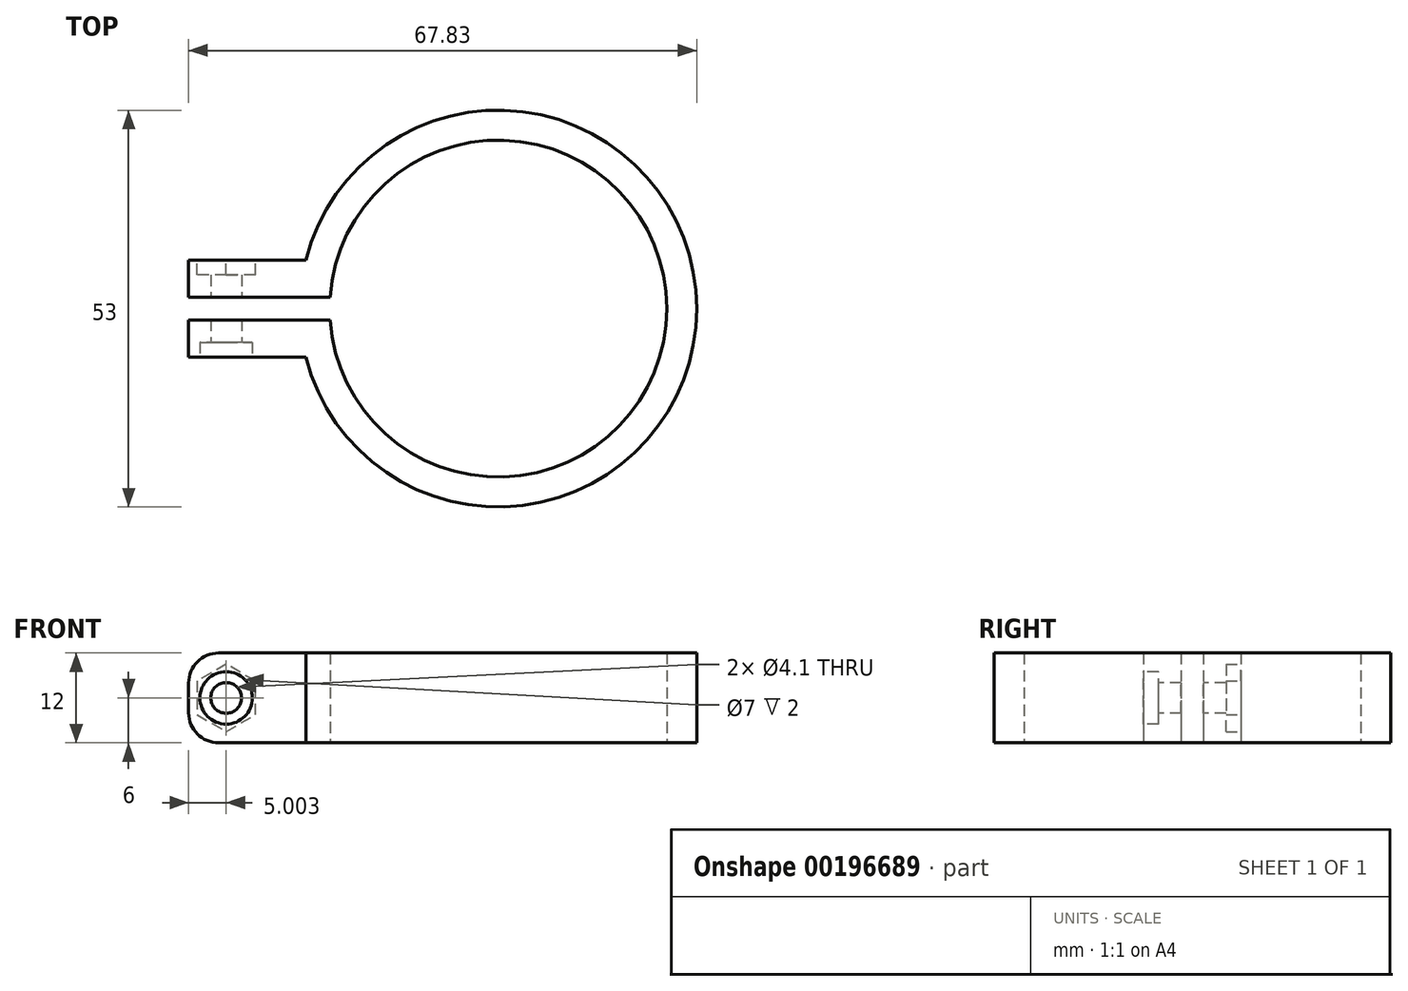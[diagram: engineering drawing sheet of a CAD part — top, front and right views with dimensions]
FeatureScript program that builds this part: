
annotation { "Feature Type Name" : "Feature", "Feature Type Description" : "" }
export const myFeature = defineFeature(function(context is Context, id is Id, definition is map)
    precondition{}
    {
        {
            var Q0;
            Q0=qCreatedBy(makeId("Top.planeOp"),FACE);
            var sketch = newSketch(context, id + "F0", { "sketchPlane" : qUnion([Q0])});
            skArc(sketch, "E0", {"start": v(-22.45, -1.5) * mm, "mid": v(22.5, 0) * mm, "end": v(-22.45, 1.5) * mm});
            skLineSegment(sketch, "E1.top", {"start": v(-25.7, -6.5) * mm, "end": v(-41.33, -6.5) * mm});
            skLineSegment(sketch, "E1.right", {"start": v(-41.33, 6.5) * mm, "end": v(-41.33, 1.5) * mm});
            skLineSegment(sketch, "E2", {"start": v(-22.45, 1.5) * mm, "end": v(-41.33, 1.5) * mm});
            skLineSegment(sketch, "E3", {"start": v(-22.45, -1.5) * mm, "end": v(-41.33, -1.5) * mm});
            skLineSegment(sketch, "E4.trimOffspring", {"start": v(-41.33, -1.5) * mm, "end": v(-41.33, -6.5) * mm});
            skLineSegment(sketch, "E5.trimOffspring", {"start": v(-25.7, 6.5) * mm, "end": v(-41.33, 6.5) * mm});
            skArc(sketch, "E6", {"start": v(-25.7, -6.5) * mm, "mid": v(26.5, 0) * mm, "end": v(-25.7, 6.5) * mm});
            skLineSegment(sketch, "E7", {"start": v(0, 0) * mm, "end": v(-55.53, 0) * mm, "construction": true});
            skSolve(sketch);
        }
        {
            var Q0;
            Q0=makeQuery(id+"F0.imprint","IMPRINT",FACE,{"disambiguationData":[TD([[makeQuery(id+"F0.imprint","IMPRINT",EDGE,{"derivedFrom":sQuery(id+"F0.wireOp",EDGE,"E0")}),-1.0]])]});
            extrude(context, id + "F1", {"entities" : qUnion([Q0]), "endBound" : BoundingType.SYMMETRIC, "depth" : 12 * mm});
        }
        {
            var Q0;
            Q0=makeQuery(id+"F1.opExtrude","SWEPT_FACE",FACE,{"disambiguationData":[OSD([sQuery(id+"F0.wireOp",EDGE,"E1.top")])]});
            var sketch = newSketch(context, id + "F2", { "sketchPlane" : qUnion([Q0])});
            skPoint(sketch, "E8", {"position": v(-33.5, 0) * mm});
            skPoint(sketch, "E8.positionSnap0", {"position": v(-41.33, 0) * mm});
            skPoint(sketch, "E8.positionSnap1", {"position": v(-33.5, 6) * mm});
            skLineSegment(sketch, "E9", {"start": v(-33.5, 0) * mm, "end": v(-41.33, 0) * mm, "construction": true});
            skPoint(sketch, "E10", {"position": v(-36.33, 0) * mm});
            skCircle(sketch, "E11", {"center": v(-36.33, 0) * mm, "radius": 2.05 * mm});
            skCircle(sketch, "E12", {"center": v(-36.33, 0) * mm, "radius": 3.5 * mm});
            skSolve(sketch);
        }
        {
            var Q0;
            Q0=makeQuery(id+"F1.opExtrude","SWEPT_FACE",FACE,{"disambiguationData":[OSD([sQuery(id+"F0.wireOp",EDGE,"E5.trimOffspring")])]});
            var sketch = newSketch(context, id + "F3", { "sketchPlane" : qUnion([Q0])});
            skPoint(sketch, "E13", {"position": v(33.5, 0) * mm});
            skPoint(sketch, "E13.positionSnap0", {"position": v(41.33, 0) * mm});
            skPoint(sketch, "E13.positionSnap1", {"position": v(33.5, 6) * mm});
            skLineSegment(sketch, "E14", {"start": v(33.5, 0) * mm, "end": v(41.33, 0) * mm, "construction": true});
            skPoint(sketch, "E15", {"position": v(36.33, 0) * mm});
            skCircle(sketch, "E16.cCircle", {"center": v(36.33, 0) * mm, "radius": 3.9 * mm, "construction": true});
            skLineSegment(sketch, "E16.0", {"start": v(40.22, 2.25) * mm, "end": v(40.22, -2.25) * mm});
            skLineSegment(sketch, "E16.1", {"start": v(40.22, -2.25) * mm, "end": v(36.33, -4.5) * mm});
            skLineSegment(sketch, "E16.2", {"start": v(36.33, -4.5) * mm, "end": v(32.43, -2.25) * mm});
            skLineSegment(sketch, "E16.3", {"start": v(32.43, -2.25) * mm, "end": v(32.43, 2.25) * mm});
            skLineSegment(sketch, "E16.4", {"start": v(32.43, 2.25) * mm, "end": v(36.33, 4.5) * mm});
            skLineSegment(sketch, "E16.5", {"start": v(36.33, 4.5) * mm, "end": v(40.22, 2.25) * mm});
            skPoint(sketch, "E16.0.midPoint", {"position": v(40.22, 0) * mm});
            skSolve(sketch);
        }
        {
            var Q0;
            Q0=makeQuery(id+"F2.imprint","IMPRINT",FACE,{"disambiguationData":[TD([[makeQuery(id+"F2.imprint","IMPRINT",EDGE,{"derivedFrom":sQuery(id+"F2.wireOp",EDGE,"E11")}),1.0]])]});
            var Q1;
            Q1=makeQuery(id+"F1.opExtrude","SWEPT_FACE",FACE,{"disambiguationData":[OSD([sQuery(id+"F0.wireOp",EDGE,"E5.trimOffspring")])]});
            extrude(context, id + "F4", {"entities" : qUnion([Q0]), "operationType" : NewBodyOperationType.REMOVE, "endBound" : BoundingType.UP_TO_SURFACE, "oppositeDirection" : true, "endBoundEntityFace" : qUnion([Q1]), "depth" : 25 * mm});
        }
        {
            var Q0;
            Q0=makeQuery(id+"F2.imprint","IMPRINT",FACE,{"disambiguationData":[TD([[makeQuery(id+"F2.imprint","IMPRINT",EDGE,{"derivedFrom":sQuery(id+"F2.wireOp",EDGE,"E11")}),-1.0]])]});
            extrude(context, id + "F5", {"entities" : qUnion([Q0]), "operationType" : NewBodyOperationType.REMOVE, "oppositeDirection" : true, "depth" : 2 * mm});
        }
        {
            var Q0;
            Q0=makeQuery(id+"F3.imprint","IMPRINT",FACE,{"disambiguationData":[TD([[makeQuery(id+"F3.imprint","IMPRINT",EDGE,{"derivedFrom":sQuery(id+"F3.wireOp",EDGE,"E16.0")}),-1.0]])]});
            extrude(context, id + "F6", {"entities" : qUnion([Q0]), "operationType" : NewBodyOperationType.REMOVE, "oppositeDirection" : true, "depth" : 2 * mm});
        }
        {
            var Q0;
            Q0=makeQuery(id+"F1.opExtrude","CAP_EDGE",EDGE,{"disambiguationData":[OSD([sQuery(id+"F0.wireOp",EDGE,"E1.right")])],"isStart":false});
            var Q1;
            Q1=makeQuery(id+"F1.opExtrude","CAP_EDGE",EDGE,{"disambiguationData":[OSD([sQuery(id+"F0.wireOp",EDGE,"E4.trimOffspring")])],"isStart":false});
            var Q2;
            Q2=makeQuery(id+"F1.opExtrude","CAP_EDGE",EDGE,{"disambiguationData":[OSD([sQuery(id+"F0.wireOp",EDGE,"E1.right")])],"isStart":true});
            var Q3;
            Q3=makeQuery(id+"F1.opExtrude","CAP_EDGE",EDGE,{"disambiguationData":[OSD([sQuery(id+"F0.wireOp",EDGE,"E4.trimOffspring")])],"isStart":true});
            fillet(context, id + "F7", {"entities" : qUnion([Q0, Q1, Q2, Q3]), "radius" : 4 * mm, "tangentPropagation" : true, "allowEdgeOverflow" : false});
        }
    });
